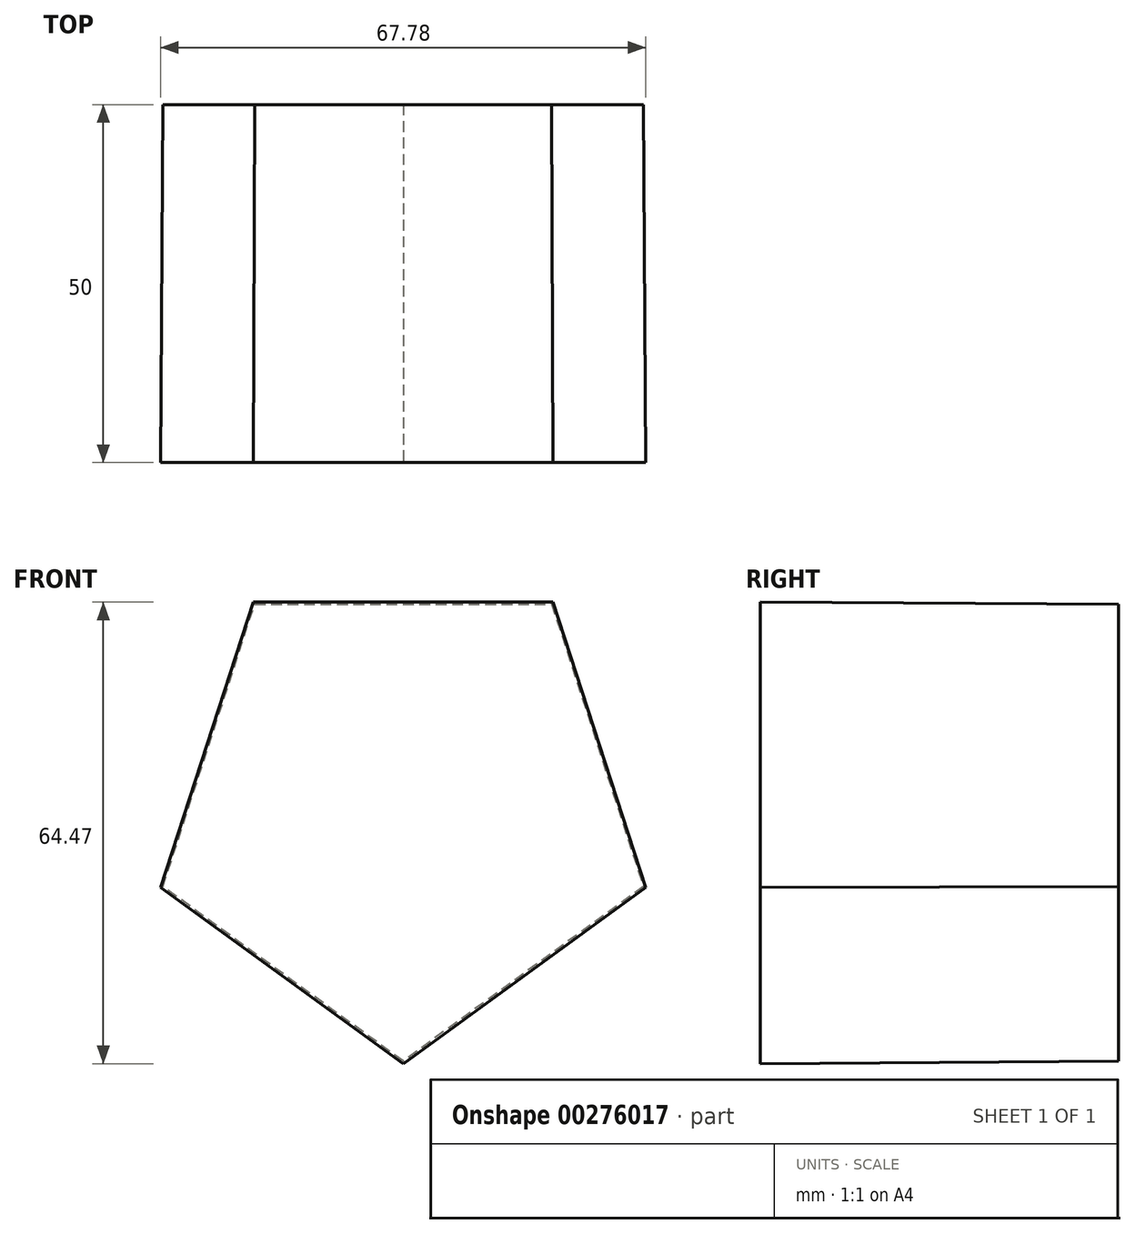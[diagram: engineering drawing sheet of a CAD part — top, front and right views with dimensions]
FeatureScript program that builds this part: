
annotation { "Feature Type Name" : "Feature", "Feature Type Description" : "" }
export const myFeature = defineFeature(function(context is Context, id is Id, definition is map)
    precondition{}
    {
        {
            var Q0;
            Q0=qCreatedBy(makeId("Front.planeOp"),FACE);
            var sketch = newSketch(context, id + "F0", { "sketchPlane" : qUnion([Q0])});
            skCircle(sketch, "E0.cCircle", {"center": v(0, 0) * mm, "radius": 28.55 * mm, "construction": true});
            skLineSegment(sketch, "E0.0", {"start": v(-20.74, 28.55) * mm, "end": v(20.74, 28.55) * mm});
            skLineSegment(sketch, "E0.1", {"start": v(20.74, 28.55) * mm, "end": v(33.56, -10.9) * mm});
            skLineSegment(sketch, "E0.2", {"start": v(33.56, -10.9) * mm, "end": v(0, -35.28) * mm});
            skLineSegment(sketch, "E0.3", {"start": v(0, -35.28) * mm, "end": v(-33.56, -10.9) * mm});
            skLineSegment(sketch, "E0.4", {"start": v(-33.56, -10.9) * mm, "end": v(-20.74, 28.55) * mm});
            skPoint(sketch, "E0.0.midPoint", {"position": v(0, 28.55) * mm});
            skSolve(sketch);
        }
        {
            var Q0;
            Q0=qCreatedBy(makeId("Front.planeOp"),FACE);
            cPlane(context, id + "F1", {"entities" : qUnion([Q0]), "cplaneType" : CPlaneType.OFFSET, "offset" : 50 * mm, "width" : 150 * mm, "height" : 150 * mm});
        }
        {
            var Q0;
            Q0=qCreatedBy(id+"F1.planeOp",FACE);
            var sketch = newSketch(context, id + "F2", { "sketchPlane" : qUnion([Q0])});
            skCircle(sketch, "E1.cCircle", {"center": v(0, 0) * mm, "radius": 28.83 * mm, "construction": true});
            skLineSegment(sketch, "E1.0", {"start": v(-20.95, 28.83) * mm, "end": v(20.95, 28.83) * mm});
            skLineSegment(sketch, "E1.1", {"start": v(20.95, 28.83) * mm, "end": v(33.9, -11.01) * mm});
            skLineSegment(sketch, "E1.2", {"start": v(33.9, -11.01) * mm, "end": v(0, -35.64) * mm});
            skLineSegment(sketch, "E1.3", {"start": v(0, -35.64) * mm, "end": v(-33.9, -11.01) * mm});
            skLineSegment(sketch, "E1.4", {"start": v(-33.9, -11.01) * mm, "end": v(-20.95, 28.83) * mm});
            skPoint(sketch, "E1.0.midPoint", {"position": v(0, 28.83) * mm});
            skSolve(sketch);
        }
        {
            var Q0;
            Q0=makeQuery(id+"F0.imprint","IMPRINT",FACE,{"disambiguationData":[TD([[makeQuery(id+"F0.imprint","IMPRINT",EDGE,{"derivedFrom":sQuery(id+"F0.wireOp",EDGE,"E0.0")}),-1.0]])]});
            var Q1;
            Q1=makeQuery(id+"F2.imprint","IMPRINT",FACE,{"disambiguationData":[TD([[makeQuery(id+"F2.imprint","IMPRINT",EDGE,{"derivedFrom":sQuery(id+"F2.wireOp",EDGE,"E1.0")}),-1.0]])]});
            loft(context, id + "F3", {"sheetProfilesArray" : [{ "sheetProfileEntities" : qUnion([Q0]) }, { "sheetProfileEntities" : qUnion([Q1]) }]});
        }
    });
